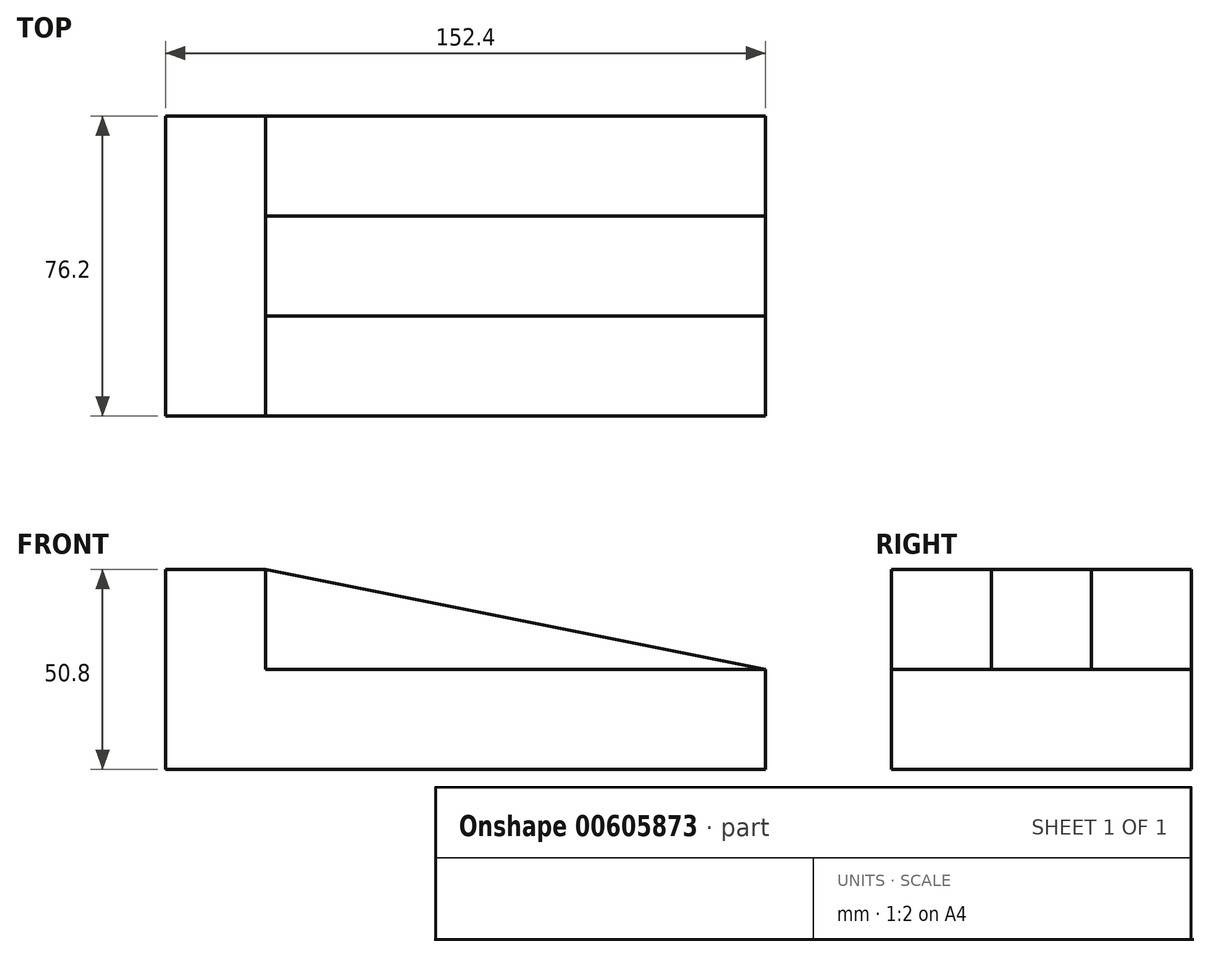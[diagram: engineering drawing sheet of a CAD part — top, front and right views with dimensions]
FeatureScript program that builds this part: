
annotation { "Feature Type Name" : "Feature", "Feature Type Description" : "" }
export const myFeature = defineFeature(function(context is Context, id is Id, definition is map)
    precondition{}
    {
        {
            var Q0;
            Q0=qCreatedBy(makeId("Front.planeOp"),FACE);
            var sketch = newSketch(context, id + "F0", { "sketchPlane" : qUnion([Q0])});
            skLineSegment(sketch, "E0", {"start": v(0, 0) * mm, "end": v(0, 50.8) * mm});
            skLineSegment(sketch, "E1", {"start": v(0, 50.8) * mm, "end": v(25.4, 50.8) * mm});
            skLineSegment(sketch, "E2", {"start": v(25.4, 50.8) * mm, "end": v(25.4, 25.4) * mm});
            skLineSegment(sketch, "E3", {"start": v(0, 0) * mm, "end": v(152.4, 0) * mm});
            skLineSegment(sketch, "E4", {"start": v(25.4, 25.4) * mm, "end": v(152.4, 25.4) * mm});
            skLineSegment(sketch, "E5", {"start": v(152.4, 25.4) * mm, "end": v(152.4, 0) * mm});
            skLineSegment(sketch, "E6", {"start": v(25.4, 50.8) * mm, "end": v(152.4, 25.4) * mm});
            skSolve(sketch);
        }
        {
            var Q0;
            Q0=makeQuery(id+"F0.imprint","IMPRINT",FACE,{"disambiguationData":[TD([[makeQuery(id+"F0.imprint","IMPRINT",EDGE,{"derivedFrom":sQuery(id+"F0.wireOp",EDGE,"E2")}),1.0]])]});
            var Q1;
            Q1=makeQuery(id+"F0.imprint","IMPRINT",FACE,{"disambiguationData":[TD([[makeQuery(id+"F0.imprint","IMPRINT",EDGE,{"derivedFrom":sQuery(id+"F0.wireOp",EDGE,"E0")}),-1.0]])]});
            extrude(context, id + "F1", {"entities" : qUnion([Q0, Q1]), "depth" : 76.2 * mm, "offsetDistance" : 25.4 * mm});
        }
        {
            var Q0;
            Q0=makeQuery(id+"F1.opExtrude","CAP_FACE",FACE,{"disambiguationData":[OSD([sQuery(id+"F0.wireOp",EDGE,"E0"),sQuery(id+"F0.wireOp",EDGE,"E1"),sQuery(id+"F0.wireOp",EDGE,"E3"),sQuery(id+"F0.wireOp",EDGE,"E5"),sQuery(id+"F0.wireOp",EDGE,"E6")])],"isStart":false});
            var sketch = newSketch(context, id + "F2", { "sketchPlane" : qUnion([Q0])});
            skLineSegment(sketch, "E7", {"start": v(25.4, 50.8) * mm, "end": v(25.4, 25.4) * mm});
            skLineSegment(sketch, "E8", {"start": v(25.4, 25.4) * mm, "end": v(152.4, 25.4) * mm});
            skSolve(sketch);
        }
        {
            var Q0;
            Q0=makeQuery(id+"F2.imprint","IMPRINT",FACE,{"disambiguationData":[TD([[makeQuery(id+"F2.imprint","IMPRINT",EDGE,{"derivedFrom":sQuery(id+"F2.wireOp",EDGE,"E7")}),1.0]])]});
            extrude(context, id + "F3", {"entities" : qUnion([Q0]), "operationType" : NewBodyOperationType.REMOVE, "oppositeDirection" : true, "depth" : 25.4 * mm, "offsetDistance" : 25.4 * mm});
        }
        {
            var Q0;
            Q0=makeQuery(id+"F1.opExtrude","CAP_FACE",FACE,{"disambiguationData":[OSD([sQuery(id+"F0.wireOp",EDGE,"E0"),sQuery(id+"F0.wireOp",EDGE,"E1"),sQuery(id+"F0.wireOp",EDGE,"E3"),sQuery(id+"F0.wireOp",EDGE,"E5"),sQuery(id+"F0.wireOp",EDGE,"E6")])],"isStart":true});
            var sketch = newSketch(context, id + "F4", { "sketchPlane" : qUnion([Q0])});
            skLineSegment(sketch, "E9", {"start": v(-25.4, 50.8) * mm, "end": v(-25.4, 25.4) * mm});
            skLineSegment(sketch, "E10", {"start": v(-25.4, 25.4) * mm, "end": v(-152.4, 25.4) * mm});
            skSolve(sketch);
        }
        {
            var Q0;
            Q0=makeQuery(id+"F4.imprint","IMPRINT",FACE,{"disambiguationData":[TD([[makeQuery(id+"F4.imprint","IMPRINT",EDGE,{"derivedFrom":sQuery(id+"F4.wireOp",EDGE,"E9")}),-1.0]])]});
            extrude(context, id + "F5", {"entities" : qUnion([Q0]), "operationType" : NewBodyOperationType.REMOVE, "oppositeDirection" : true, "depth" : 25.4 * mm, "offsetDistance" : 25.4 * mm});
        }
    });
